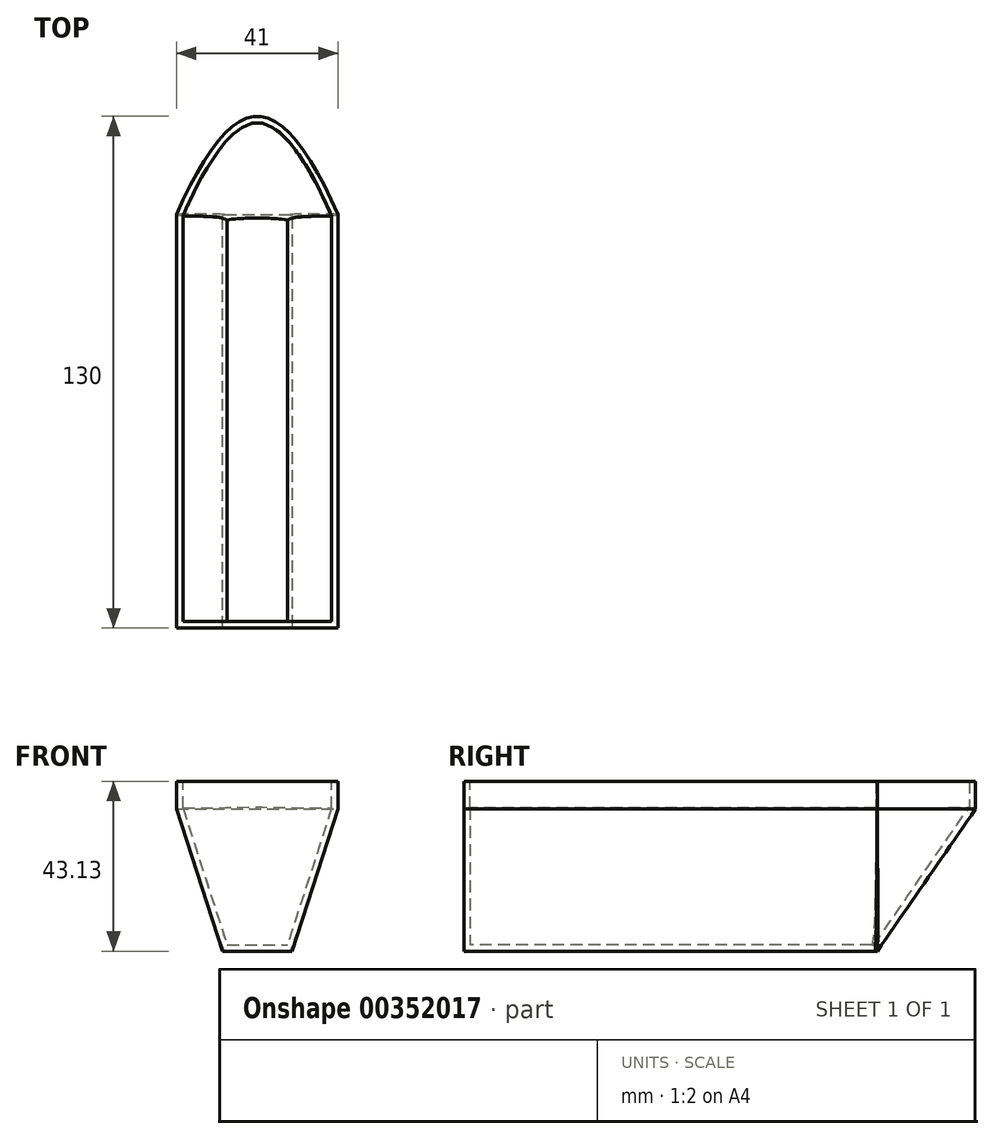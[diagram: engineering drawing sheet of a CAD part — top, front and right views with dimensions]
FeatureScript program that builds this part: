
annotation { "Feature Type Name" : "Feature", "Feature Type Description" : "" }
export const myFeature = defineFeature(function(context is Context, id is Id, definition is map)
    precondition{}
    {
        {
            var Q0;
            Q0=qCreatedBy(makeId("Top.planeOp"),FACE);
            cPlane(context, id + "F0", {"entities" : qUnion([Q0]), "cplaneType" : CPlaneType.OFFSET, "offset" : 36.12 * mm, "width" : 150 * mm, "height" : 150 * mm});
        }
        {
            var Q0;
            Q0=qCreatedBy(id+"F0.planeOp",FACE);
            var sketch = newSketch(context, id + "F1", { "sketchPlane" : qUnion([Q0])});
            skLineSegment(sketch, "E0", {"start": v(-20.5, 0) * mm, "end": v(-20.5, -105) * mm});
            skLineSegment(sketch, "E1", {"start": v(-20.5, -105) * mm, "end": v(20.5, -105) * mm});
            skLineSegment(sketch, "E2", {"start": v(20.5, -105) * mm, "end": v(20.5, 0) * mm});
            skPoint(sketch, "E3", {"position": v(0, 25) * mm});
            skFitSpline(sketch, "E4", {"points": [v(-20.5, 0) * mm, v(0, 25) * mm, v(20.5, 0) * mm], "startDerivative": vector(39, 90) * mm, "endDerivative": vector(39, -90) * mm});
            skSolve(sketch);
        }
        {
            var Q0;
            Q0=qCreatedBy(makeId("Top.planeOp"),FACE);
            var sketch = newSketch(context, id + "F2", { "sketchPlane" : qUnion([Q0])});
            skLineSegment(sketch, "E5", {"start": v(8.83, 0) * mm, "end": v(8.83, -105) * mm});
            skLineSegment(sketch, "E6", {"start": v(8.83, -105) * mm, "end": v(-8.83, -105) * mm});
            skLineSegment(sketch, "E7", {"start": v(-8.83, -105) * mm, "end": v(-8.83, 0) * mm});
            skLineSegment(sketch, "E8", {"start": v(-8.83, 0) * mm, "end": v(8.83, 0) * mm});
            skSolve(sketch);
        }
        {
            var Q0;
            Q0=makeQuery(id+"F1.imprint","IMPRINT",FACE,{"disambiguationData":[TD([[makeQuery(id+"F1.imprint","IMPRINT",EDGE,{"derivedFrom":sQuery(id+"F1.wireOp",EDGE,"E0")}),1.0]])]});
            var Q1;
            Q1=makeQuery(id+"F2.imprint","IMPRINT",FACE,{"disambiguationData":[TD([[makeQuery(id+"F2.imprint","IMPRINT",EDGE,{"derivedFrom":sQuery(id+"F2.wireOp",EDGE,"E5")}),-1.0]])]});
            loft(context, id + "F3", {"sheetProfilesArray" : [{ "sheetProfileEntities" : qUnion([Q0]) }, { "sheetProfileEntities" : qUnion([Q1]) }]});
        }
        {
            var Q0;
            Q0=makeQuery(id+"F3.opLoft","CAP_FACE",FACE,{"disambiguationData":[OSD([makeQuery(id+"F1.imprint","IMPRINT",FACE,{"disambiguationData":[TD([[makeQuery(id+"F1.imprint","IMPRINT",EDGE,{"derivedFrom":sQuery(id+"F1.wireOp",EDGE,"E0")}),1.0]])]})])],"isStart":true});
            extrude(context, id + "F4", {"entities" : qUnion([Q0]), "operationType" : NewBodyOperationType.ADD, "depth" : 7 * mm});
        }
        {
            var Q0;
            Q0=makeQuery(id+"F4.opExtrude","CAP_FACE",FACE,{"disambiguationData":[OSD([makeQuery(id+"F1.imprint","IMPRINT",FACE,{"disambiguationData":[TD([[makeQuery(id+"F1.imprint","IMPRINT",EDGE,{"derivedFrom":sQuery(id+"F1.wireOp",EDGE,"E0")}),1.0]])]})])],"isStart":false});
            shell(context, id + "F5", {"entities" : qUnion([Q0]), "thickness" : 1.6 * mm});
        }
        {
            var Q0;
            Q0=makeQuery(id+"F3.opLoft","SWEPT_EDGE",EDGE,{"disambiguationData":[OSD([sQuery(id+"F1.wireOp",EDGE,"E2"),sQuery(id+"F1.wireOp",EDGE,"E4"),sQuery(id+"F2.wireOp",EDGE,"E5"),sQuery(id+"F2.wireOp",EDGE,"E8")])]});
            var Q1;
            Q1=makeQuery(id+"F3.opLoft","SWEPT_EDGE",EDGE,{"disambiguationData":[OSD([sQuery(id+"F1.wireOp",EDGE,"E0"),sQuery(id+"F1.wireOp",EDGE,"E4"),sQuery(id+"F2.wireOp",EDGE,"E7"),sQuery(id+"F2.wireOp",EDGE,"E8")])]});
            fillet(context, id + "F6", {"entities" : qUnion([Q0, Q1]), "radius" : .5 * mm, "tangentPropagation" : true, "allowEdgeOverflow" : false});
        }
    });
